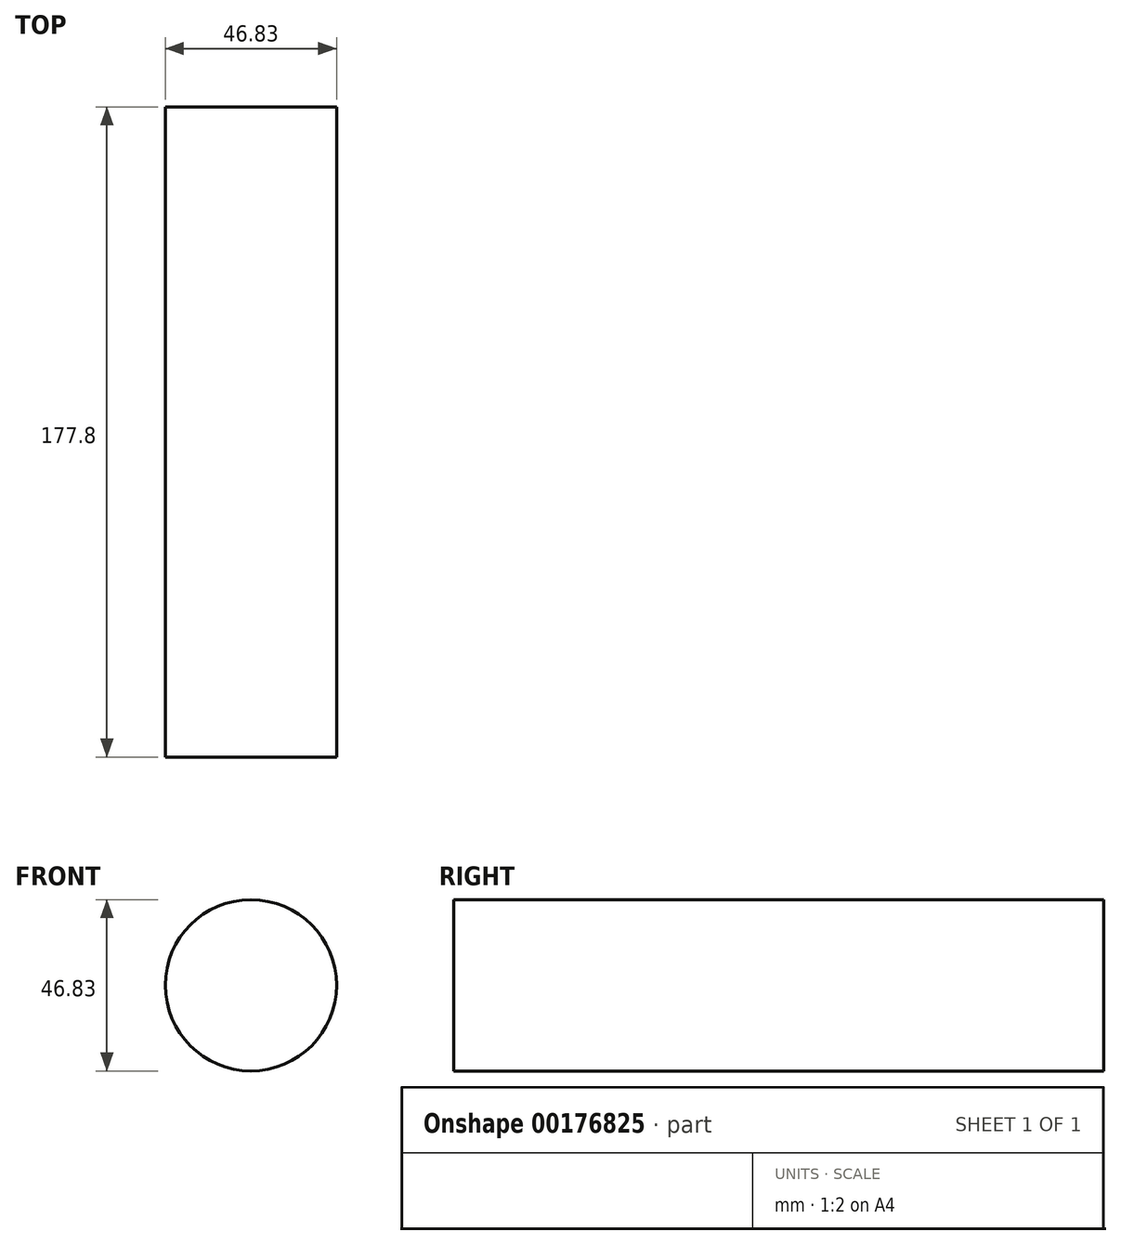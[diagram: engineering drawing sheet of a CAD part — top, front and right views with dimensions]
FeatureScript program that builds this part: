
annotation { "Feature Type Name" : "Feature", "Feature Type Description" : "" }
export const myFeature = defineFeature(function(context is Context, id is Id, definition is map)
    precondition{}
    {
        {
            var Q0;
            Q0=qCreatedBy(makeId("Front.planeOp"),FACE);
            var sketch = newSketch(context, id + "F0", { "sketchPlane" : qUnion([Q0])});
            skCircle(sketch, "E0", {"center": v(-31.48, 21.58) * mm, "radius": 23.41 * mm});
            skSolve(sketch);
        }
        {
            var Q0;
            Q0=makeQuery(id+"F0.imprint","IMPRINT",FACE,{"disambiguationData":[TD([[makeQuery(id+"F0.imprint","IMPRINT",EDGE,{"derivedFrom":sQuery(id+"F0.wireOp",EDGE,"E0")}),1.0]])]});
            extrude(context, id + "F1", {"entities" : qUnion([Q0]), "depth" : 177.8 * mm});
        }
        {
            var Q0;
            Q0=makeQuery(id+"F1.opExtrude","CAP_FACE",FACE,{"disambiguationData":[OSD([sQuery(id+"F0.wireOp",EDGE,"E0")])],"isStart":false});
            var sketch = newSketch(context, id + "F2", { "sketchPlane" : qUnion([Q0])});
            skCircle(sketch, "E1", {"center": v(-35.38, 28.08) * mm, "radius": 8.31 * mm});
            skSolve(sketch);
        }
    });
